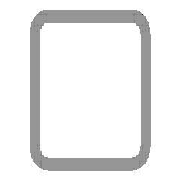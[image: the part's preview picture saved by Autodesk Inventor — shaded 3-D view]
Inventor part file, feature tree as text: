
AUTODESK INVENTOR PART (.ipt)
format: ipt  version: 2025.1 (Build 291241020, 241B)  size: 133,632 bytes
history: native  units: mm (DEFAULTED — no unit token found)
features: other x4, sketch x1, plane x1
ambient origin geometry x8: Origin, YZ Plane, XZ Plane, XY Plane, X Axis, Y Axis, Z Axis, Center Point
bodies: Solid1 (feature_tree), Body (feature_tree)
feature tree (6):
  parser-record x1  (decoder bookkeeping rows leaked as tree rows — omitted from the tree; the rows remain in map.json)
  other  "Driven Length"
  other  "Start Plane"
  other  "End Plane"
  sketch  "Sketch3"  dims[d3=660.0mm d4=0.0mm d7=4.0mm d9=40.0mm d11=40.0mm d12=2.0mm d13=20.0mm d14=680.0mm d15=20.0mm d16=20.0mm d17=90.0deg d18=660.0mm]
  plane  "Work Plane3"
